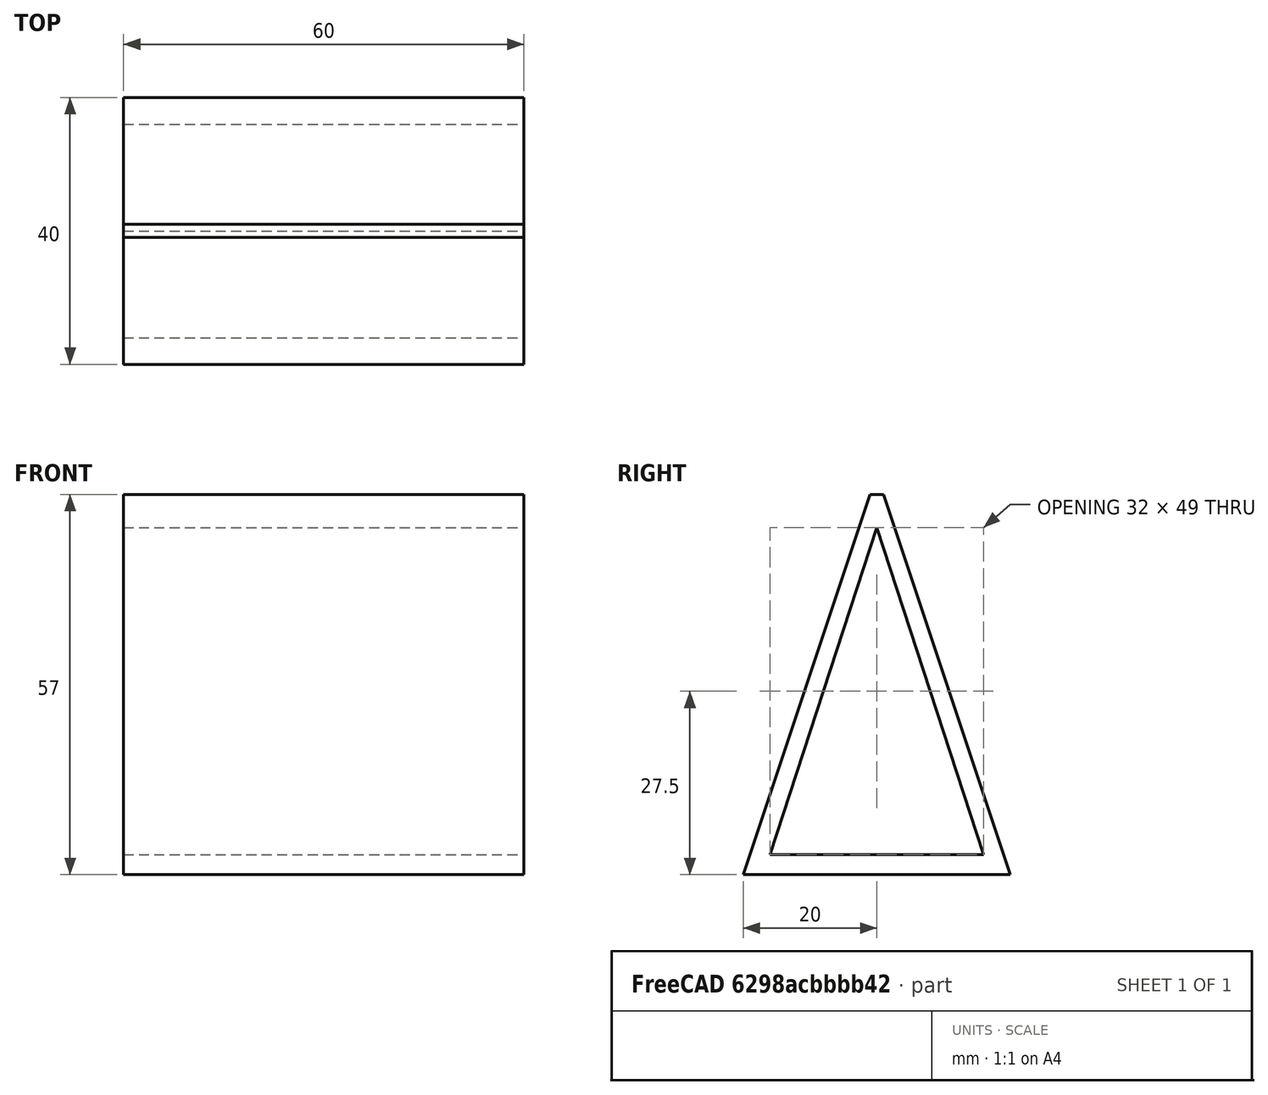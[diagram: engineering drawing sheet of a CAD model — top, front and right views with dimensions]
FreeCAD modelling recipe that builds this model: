
FCSTD DOCUMENT  (FreeCAD 1.0R39109 (Git))
Label: panel_stand
License: All rights reserved
LicenseURL: http://en.wikipedia.org/wiki/All_rights_reserved
objects: Sketcher::SketchObject×1, PartDesign::Pad×1, PartDesign::Body×1
note: 6 computed .brp shape members not serialized (recipe doc carries the construction recipe); baked Part::Feature solids carry a one-line shape summary decoded from their .brp

FEATURE [Sketcher::SketchObject] Sketch  label="Side-Sketch"
  ArcFitTolerance = 0
  AttachmentSupport = -> [YZ_Plane]
  FullyConstrained = true
  MakeInternals = false
  MapMode = 5
  Placement = pos=(0,0,0) rot=(0.57735,0.57735,0.57735;2.0944rad)
  sketch-geometry (11):
    g0: LineSegment StartX=-20 StartY=0 StartZ=0 EndX=20 EndY=2.3e-15 EndZ=0
    g1: LineSegment StartX=-16 StartY=3 StartZ=0 EndX=16 EndY=3 EndZ=0
    g2: LineSegment StartX=0 StartY=52 StartZ=0 EndX=-16 EndY=3 EndZ=0
    g3: LineSegment StartX=0 StartY=52 StartZ=0 EndX=16 EndY=3 EndZ=0
    g4: GeomPoint [constr] X=0 Y=3 Z=0
    g5: GeomPoint X=-1 Y=57 Z=0
    g6: GeomPoint X=1 Y=57 Z=0
    g7: GeomPoint X=0 Y=60 Z=0
    g8: LineSegment StartX=-1 StartY=57 StartZ=0 EndX=1 EndY=57 EndZ=0
    g9: LineSegment StartX=1 StartY=57 StartZ=0 EndX=20 EndY=2.3e-15 EndZ=0
    g10: LineSegment StartX=-20 StartY=0 StartZ=0 EndX=-1 EndY=57 EndZ=0
  constraints (25):
    c: PointOnObject(g0,g-1)
    c: Symmetric(g0,g0,g-1)
    c: DistanceX(g0,g0) = 40
    c: PointOnObject(g7,g-2)
    c: DistanceY(g-1,g7) = 60
    c: Horizontal(g1)
    c: Coincident(g2,g1)
    c: Coincident(g3,g2)
    c: Coincident(g3,g1)
    c: DistanceY(g0,g1) = 3
    c: DistanceX(g0,g1) = 4
    c: PointOnObject(g4,g-2)
    c: Symmetric(g1,g1,g4)
    c: DistanceY(g2,g7) = 8
    c: Horizontal(g5,g6)
    c: Coincident(g8,g5)
    c: Coincident(g8,g6)
    c: Coincident(g9,g6)
    c: Coincident(g9,g0)
    c: Coincident(g10,g0)
    c: Coincident(g10,g5)
    c: PointOnObject(g7,g9)
    c: PointOnObject(g7,g10)
    c: DistanceX(g8,g8) = 2
    c: PointOnObject(g2,g-2)
FEATURE [PartDesign::Pad] Pad
  Direction = (1,0,0)
  Length = 60
  Length2 = 10
  Placement = pos=(0,0,0) rot=(1,1,1;2.0944rad)
  Profile = -> Sketch
  ReferenceAxis = -> Sketch [N_Axis]
  Suppressed = false
  Type = 0
FEATURE [PartDesign::Body] Body  label="main"
  AllowCompound = false
  Group = -> [Sketch,Pad]
  Origin = -> Origin
  Tip = -> Pad
